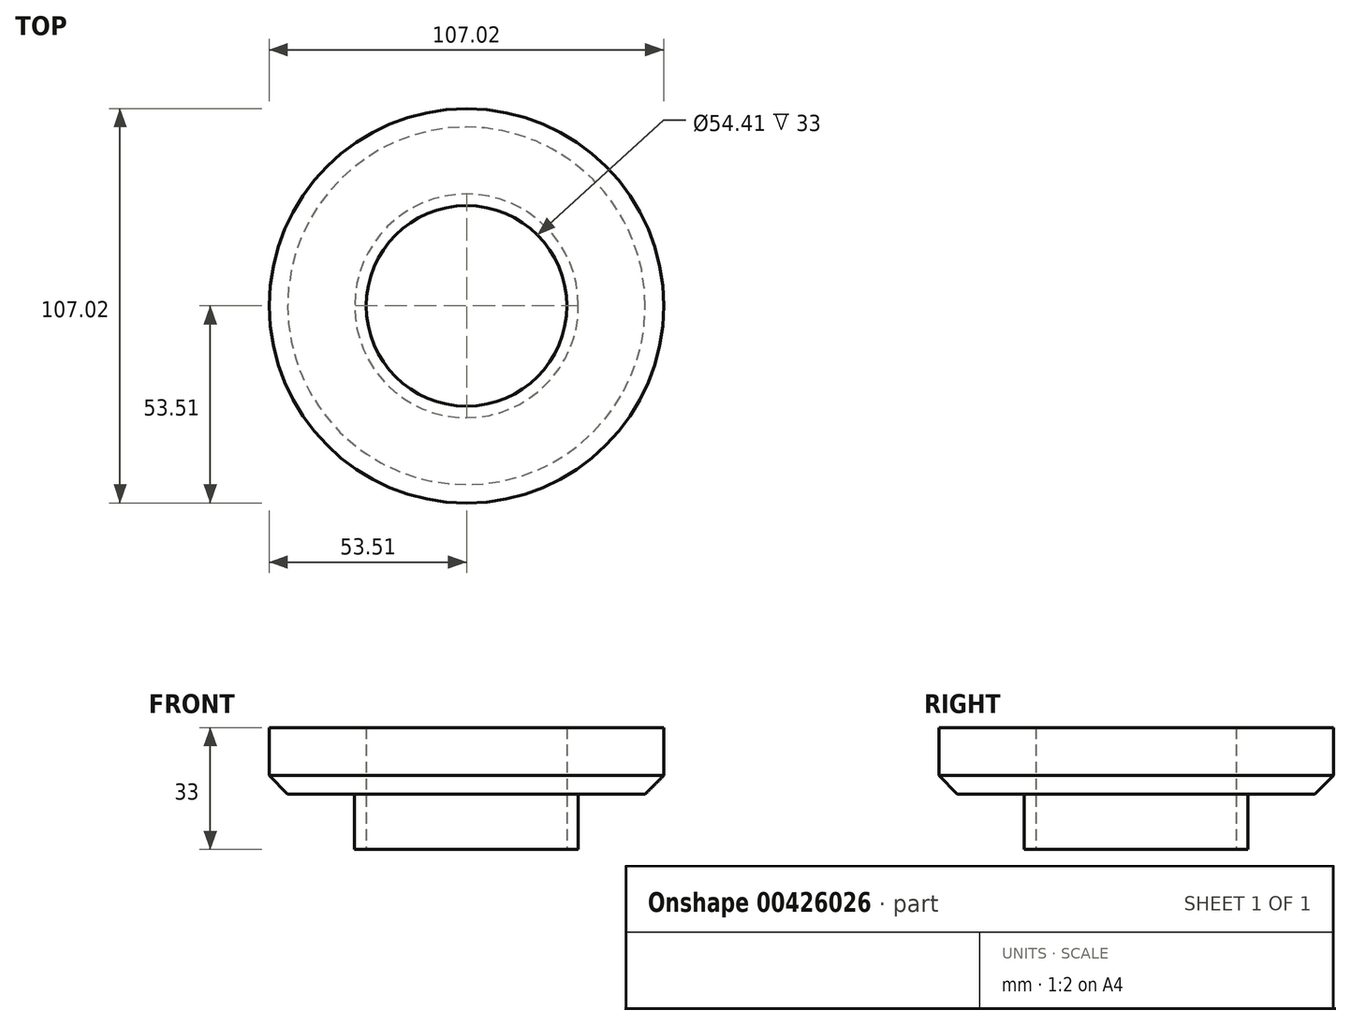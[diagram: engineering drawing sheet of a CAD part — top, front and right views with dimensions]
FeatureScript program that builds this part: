
annotation { "Feature Type Name" : "Feature", "Feature Type Description" : "" }
export const myFeature = defineFeature(function(context is Context, id is Id, definition is map)
    precondition{}
    {
        {
            var Q0;
            Q0=qCreatedBy(makeId("Top.planeOp"),FACE);
            var sketch = newSketch(context, id + "F0", { "sketchPlane" : qUnion([Q0])});
            skCircle(sketch, "E0", {"center": v(0, 0) * mm, "radius": 27.2 * mm});
            skCircle(sketch, "E1", {"center": v(0, 0) * mm, "radius": 30.35 * mm});
            skSolve(sketch);
        }
        {
            var Q0;
            Q0 = qSketchRegion(id + "F0", true);
            extrude(context, id + "F1", {"entities" : qUnion([Q0]), "depth" : 15 * mm});
        }
        {
            var Q0;
            Q0=makeQuery(id+"F1.opExtrude","CAP_FACE",FACE,{"disambiguationData":[OSD([sQuery(id+"F0.wireOp",EDGE,"E0"),sQuery(id+"F0.wireOp",EDGE,"E1")])],"isStart":false});
            var sketch = newSketch(context, id + "F2", { "sketchPlane" : qUnion([Q0])});
            skCircle(sketch, "E2", {"center": v(0, 0) * mm, "radius": 53.51 * mm});
            skSolve(sketch);
        }
        {
            var Q0;
            Q0 = qSketchRegion(id + "F2", true);
            extrude(context, id + "F3", {"entities" : qUnion([Q0]), "operationType" : NewBodyOperationType.ADD, "depth" : 18 * mm});
        }
        {
            var Q0;
            Q0=makeQuery(id+"F0.imprint","IMPRINT",FACE,{"disambiguationData":[TD([[makeQuery(id+"F0.imprint","IMPRINT",EDGE,{"derivedFrom":sQuery(id+"F0.wireOp",EDGE,"E0")}),1.0]])]});
            extrude(context, id + "F4", {"entities" : qUnion([Q0]), "operationType" : NewBodyOperationType.REMOVE, "depth" : 81.4 * mm});
        }
        {
            var Q0;
            Q0=makeQuery(id+"F3.opExtrude","CAP_EDGE",EDGE,{"disambiguationData":[OSD([sQuery(id+"F2.wireOp",EDGE,"E2")])],"isStart":true});
            chamfer(context, id + "F5", {"entities" : qUnion([Q0]), "width" : 5 * mm, "tangentPropagation" : true});
        }
    });
